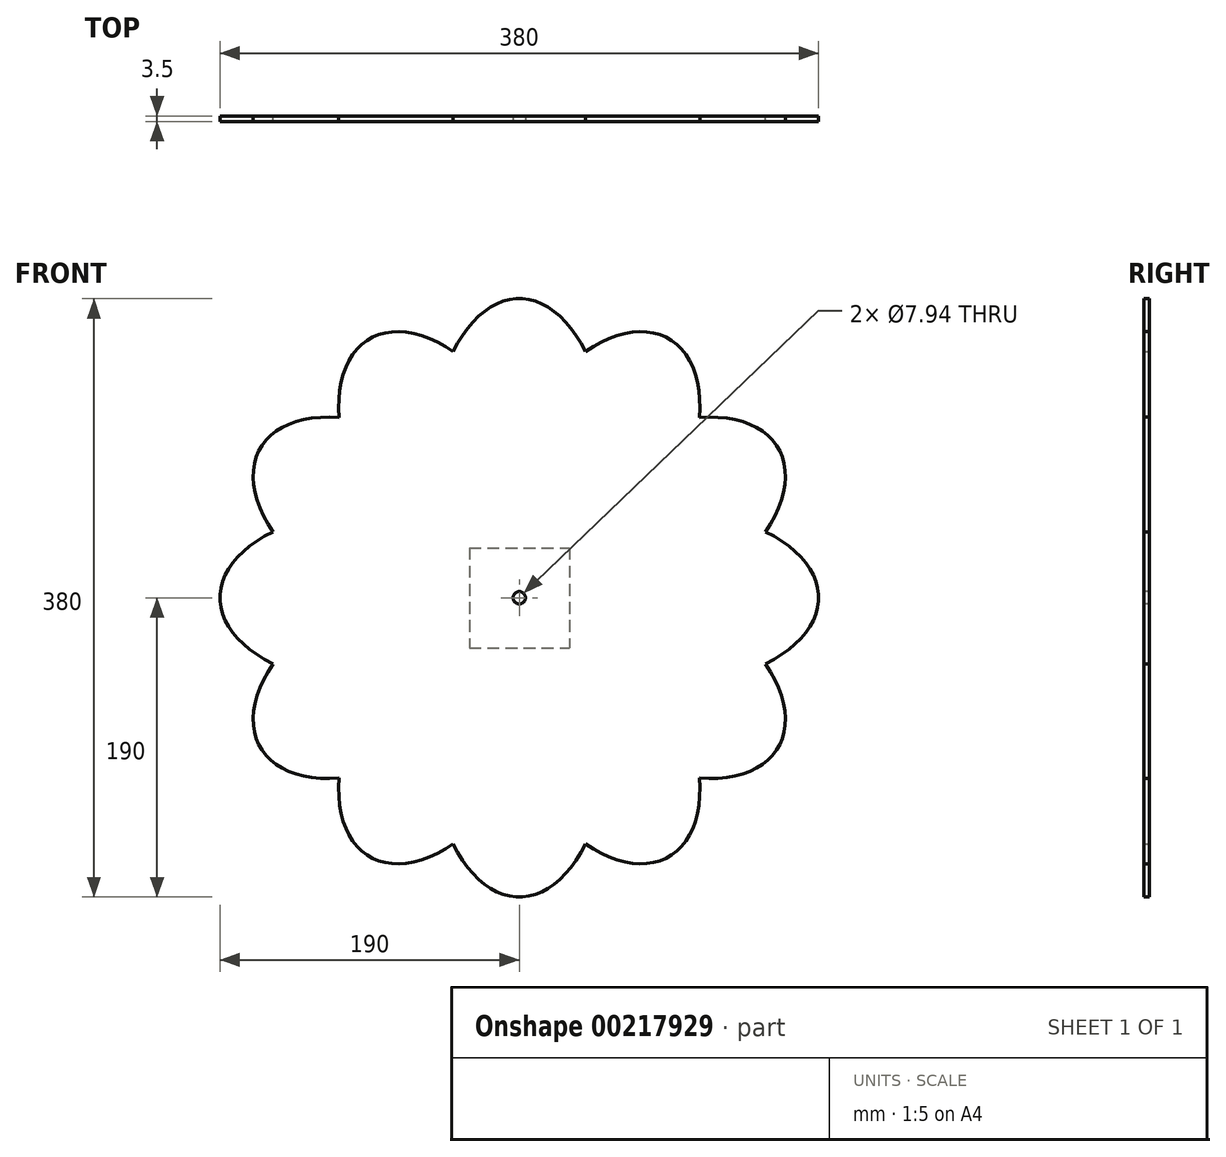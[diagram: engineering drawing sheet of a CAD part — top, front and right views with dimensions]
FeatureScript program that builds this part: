
annotation { "Feature Type Name" : "Feature", "Feature Type Description" : "" }
export const myFeature = defineFeature(function(context is Context, id is Id, definition is map)
    precondition{}
    {
        {
            var Q0;
            Q0=qCreatedBy(makeId("Front.planeOp"),FACE);
            var sketch = newSketch(context, id + "F0", { "sketchPlane" : qUnion([Q0])});
            skEllipse(sketch, "E0", {"center": v(0, 95) * mm, "majorRadius": 95 * mm, "minorRadius": 55 * mm, "majorAxis": v(0, -1)});
            skPoint(sketch, "E1.center", {"position": v(0, 0) * mm});
            skFitSpline(sketch, "E2.0", {"points": [v(-1.45, 15.04) * mm, v(0, 14.98) * mm, v(1.45, 15.04) * mm, v(3.38, 15.29) * mm, v(5.86, 15.92) * mm, v(9, 17.27) * mm, v(12.3, 19.3) * mm, v(15.72, 22.09) * mm, v(19.2, 25.66) * mm, v(22.05, 29.3) * mm, v(24.28, 32.62) * mm, v(25.92, 35.31) * mm, v(27.5, 38.18) * mm, v(29.5, 42.2) * mm, v(31.82, 47.6) * mm, v(34.25, 54.62) * mm, v(36.3, 62.08) * mm, v(37.92, 69.92) * mm, v(38.91, 76.7) * mm, v(39.47, 82.26) * mm, v(39.78, 86.46) * mm, v(39.93, 90) * mm, v(39.99, 92.86) * mm, v(40, 95) * mm, v(39.99, 97.14) * mm, v(39.93, 100) * mm, v(39.78, 103.54) * mm, v(39.47, 107.74) * mm, v(38.91, 113.3) * mm, v(37.92, 120.08) * mm, v(36.3, 127.92) * mm, v(34.25, 135.38) * mm, v(31.82, 142.4) * mm, v(29.5, 147.8) * mm, v(27.5, 151.82) * mm, v(25.92, 154.69) * mm, v(24.28, 157.38) * mm, v(22.05, 160.7) * mm, v(19.2, 164.34) * mm, v(15.72, 167.91) * mm, v(12.3, 170.7) * mm, v(9, 172.73) * mm, v(5.86, 174.08) * mm, v(3.38, 174.71) * mm, v(1.45, 174.96) * mm, v(0, 175.02) * mm, v(-1.45, 174.96) * mm, v(-3.38, 174.71) * mm, v(-5.86, 174.08) * mm, v(-9, 172.73) * mm, v(-12.3, 170.7) * mm, v(-15.72, 167.91) * mm, v(-19.2, 164.34) * mm, v(-22.05, 160.7) * mm, v(-24.28, 157.38) * mm, v(-25.92, 154.69) * mm, v(-27.5, 151.82) * mm, v(-29.5, 147.8) * mm, v(-31.82, 142.4) * mm, v(-34.25, 135.38) * mm, v(-36.3, 127.92) * mm, v(-37.92, 120.08) * mm, v(-38.91, 113.3) * mm, v(-39.47, 107.74) * mm, v(-39.78, 103.54) * mm, v(-39.93, 100) * mm, v(-39.99, 97.14) * mm, v(-40, 95) * mm, v(-39.99, 92.86) * mm, v(-39.93, 90) * mm, v(-39.78, 86.46) * mm, v(-39.47, 82.26) * mm, v(-38.91, 76.7) * mm, v(-37.92, 69.92) * mm, v(-36.3, 62.08) * mm, v(-34.25, 54.62) * mm, v(-31.82, 47.6) * mm, v(-29.5, 42.2) * mm, v(-27.5, 38.18) * mm, v(-25.92, 35.31) * mm, v(-24.28, 32.62) * mm, v(-22.05, 29.3) * mm, v(-19.2, 25.66) * mm, v(-15.72, 22.09) * mm, v(-12.3, 19.3) * mm, v(-9, 17.27) * mm, v(-5.86, 15.92) * mm, v(-3.38, 15.29) * mm, v(-1.45, 15.04) * mm, v(0, 14.98) * mm, v(1.45, 15.04) * mm, v(-1.45, 15.04) * mm]});
            skSolve(sketch);
        }
        {
            var Q0;
            Q0=makeQuery(id+"F0.imprint","IMPRINT",FACE,{"disambiguationData":[TD([[makeQuery(id+"F0.imprint","IMPRINT",EDGE,{"derivedFrom":sQuery(id+"F0.wireOp",EDGE,"E0")}),1.0]])]});
            extrude(context, id + "F1", {"entities" : qUnion([Q0]), "depth" : 3.48 * mm});
        }
        {
            var Q0;
            Q0=qCreatedBy(makeId("Right.planeOp"),FACE);
            var sketch = newSketch(context, id + "F2", { "sketchPlane" : qUnion([Q0])});
            skLineSegment(sketch, "E3", {"start": v(0, 0) * mm, "end": v(-41.22, 0) * mm});
            skSolve(sketch);
        }
        {
            var Q0;
            Q0=makeQuery(id+"F1.opExtrude","SWEPT_BODY",BODY,{"disambiguationData":[OSD([sQuery(id+"F0.wireOp",EDGE,"E0"),sQuery(id+"F0.wireOp",EDGE,"E2.0")])]});
            var Q1;
            Q1=sQuery(id+"F2.wireOp",EDGE,"E3");
            circularPattern(context, id + "F3", {"operationType" : NewBodyOperationType.ADD, "entities" : qUnion([Q0]), "axis" : qUnion([Q1]), "angle" : 360 * degree, "instanceCount" : 12, "equalSpace" : true});
        }
        {
            var Q0;
            Q0=qCreatedBy(makeId("Front.planeOp"),FACE);
            var sketch = newSketch(context, id + "F4", { "sketchPlane" : qUnion([Q0])});
            skFitSpline(sketch, "E4.0", {"points": [v(10, 17.32) * mm, v(10.54, 17) * mm, v(11.65, 16.43) * mm, v(13.42, 15.72) * mm, v(15.32, 15.14) * mm, v(18.06, 14.55) * mm, v(21.93, 14.2) * mm, v(27.37, 14.55) * mm, v(33.58, 15.79) * mm, v(39.31, 17.66) * mm, v(44.19, 19.7) * mm, v(47.97, 21.5) * mm, v(51.22, 23.23) * mm, v(53.87, 24.76) * mm, v(55.88, 25.98) * mm, v(57.91, 27.26) * mm, v(60.62, 29.07) * mm, v(64.04, 31.47) * mm, v(68.15, 34.61) * mm, v(73.63, 39.1) * mm, v(80.46, 45.3) * mm, v(88.51, 53.59) * mm, v(96.35, 62.64) * mm, v(102.62, 70.77) * mm, v(107.45, 77.58) * mm, v(110.97, 82.83) * mm, v(113.8, 87.32) * mm, v(116.01, 90.97) * mm, v(117.64, 93.74) * mm, v(119.23, 96.53) * mm, v(121.28, 100.27) * mm, v(123.75, 104.97) * mm, v(126.54, 110.64) * mm, v(130.03, 118.23) * mm, v(133.93, 127.73) * mm, v(137.85, 139.04) * mm, v(141, 150.16) * mm, v(142.95, 159.17) * mm, v(144.1, 166.17) * mm, v(144.76, 171.3) * mm, v(145.14, 175.45) * mm, v(145.34, 178.7) * mm, v(145.44, 181.1) * mm, v(145.5, 183.45) * mm, v(145.5, 186.51) * mm, v(145.37, 190.2) * mm, v(145.04, 194.37) * mm, v(144.37, 199.61) * mm, v(143.12, 205.51) * mm, v(141.09, 211.5) * mm, v(138.66, 216.39) * mm, v(136.43, 219.57) * mm, v(134.55, 221.66) * mm, v(133.1, 223.01) * mm, v(131.6, 224.18) * mm, v(130.01, 225.2) * mm, v(128.35, 226.05) * mm, v(126.58, 226.77) * mm, v(124.68, 227.35) * mm, v(121.94, 227.93) * mm, v(118.07, 228.28) * mm, v(112.63, 227.94) * mm, v(106.42, 226.7) * mm, v(100.69, 224.83) * mm, v(95.81, 222.8) * mm, v(92.03, 221) * mm, v(88.78, 219.26) * mm, v(86.13, 217.73) * mm, v(84.12, 216.5) * mm, v(82.09, 215.22) * mm, v(79.38, 213.42) * mm, v(75.96, 211.01) * mm, v(71.85, 207.88) * mm, v(66.37, 203.38) * mm, v(59.54, 197.18) * mm, v(51.49, 188.9) * mm, v(43.65, 179.85) * mm, v(37.38, 171.72) * mm, v(32.55, 164.91) * mm, v(29.03, 159.66) * mm, v(26.2, 155.17) * mm, v(23.99, 151.52) * mm, v(22.36, 148.75) * mm, v(20.77, 145.95) * mm, v(18.72, 142.22) * mm, v(16.25, 137.52) * mm, v(13.46, 131.84) * mm, v(9.97, 124.26) * mm, v(6.07, 114.76) * mm, v(2.15, 103.45) * mm, v(-1, 92.33) * mm, v(-2.95, 83.32) * mm, v(-4.1, 76.32) * mm, v(-4.76, 71.2) * mm, v(-5.14, 67.03) * mm, v(-5.34, 63.78) * mm, v(-5.44, 61.38) * mm, v(-5.5, 59.03) * mm, v(-5.5, 55.97) * mm, v(-5.37, 52.3) * mm, v(-5.04, 48.11) * mm, v(-4.37, 42.88) * mm, v(-3.12, 36.97) * mm, v(-1.09, 30.98) * mm, v(1.34, 26.1) * mm, v(3.57, 22.92) * mm, v(5.45, 20.83) * mm, v(6.9, 19.48) * mm, v(8.4, 18.3) * mm, v(9.46, 17.63) * mm, v(10, 17.32) * mm]});
            skFitSpline(sketch, "E4.1", {"points": [v(-10, 17.32) * mm, v(-9.46, 17.63) * mm, v(-8.4, 18.3) * mm, v(-6.9, 19.48) * mm, v(-5.45, 20.83) * mm, v(-3.57, 22.92) * mm, v(-1.34, 26.1) * mm, v(1.09, 30.98) * mm, v(3.12, 36.97) * mm, v(4.37, 42.88) * mm, v(5.04, 48.11) * mm, v(5.37, 52.3) * mm, v(5.5, 55.97) * mm, v(5.5, 59.03) * mm, v(5.44, 61.38) * mm, v(5.34, 63.78) * mm, v(5.14, 67.03) * mm, v(4.76, 71.2) * mm, v(4.1, 76.32) * mm, v(2.95, 83.32) * mm, v(1, 92.33) * mm, v(-2.15, 103.45) * mm, v(-6.07, 114.76) * mm, v(-9.97, 124.26) * mm, v(-13.46, 131.84) * mm, v(-16.25, 137.52) * mm, v(-18.72, 142.22) * mm, v(-20.77, 145.95) * mm, v(-22.36, 148.75) * mm, v(-23.99, 151.52) * mm, v(-26.2, 155.17) * mm, v(-29.03, 159.66) * mm, v(-32.55, 164.91) * mm, v(-37.38, 171.72) * mm, v(-43.65, 179.85) * mm, v(-51.49, 188.9) * mm, v(-59.54, 197.18) * mm, v(-66.37, 203.38) * mm, v(-71.85, 207.88) * mm, v(-75.96, 211.01) * mm, v(-79.38, 213.42) * mm, v(-82.09, 215.22) * mm, v(-84.12, 216.5) * mm, v(-86.13, 217.73) * mm, v(-88.78, 219.26) * mm, v(-92.03, 221) * mm, v(-95.81, 222.8) * mm, v(-100.69, 224.83) * mm, v(-106.42, 226.7) * mm, v(-112.63, 227.94) * mm, v(-118.07, 228.28) * mm, v(-121.94, 227.93) * mm, v(-124.68, 227.35) * mm, v(-126.58, 226.77) * mm, v(-128.35, 226.05) * mm, v(-130.01, 225.2) * mm, v(-131.6, 224.18) * mm, v(-133.1, 223.01) * mm, v(-134.55, 221.66) * mm, v(-136.43, 219.57) * mm, v(-138.66, 216.39) * mm, v(-141.09, 211.5) * mm, v(-143.12, 205.51) * mm, v(-144.37, 199.61) * mm, v(-145.04, 194.37) * mm, v(-145.37, 190.2) * mm, v(-145.5, 186.51) * mm, v(-145.5, 183.45) * mm, v(-145.44, 181.1) * mm, v(-145.34, 178.7) * mm, v(-145.14, 175.45) * mm, v(-144.76, 171.3) * mm, v(-144.1, 166.17) * mm, v(-142.95, 159.17) * mm, v(-141, 150.16) * mm, v(-137.85, 139.04) * mm, v(-133.93, 127.73) * mm, v(-130.03, 118.23) * mm, v(-126.54, 110.64) * mm, v(-123.75, 104.97) * mm, v(-121.28, 100.27) * mm, v(-119.23, 96.53) * mm, v(-117.64, 93.74) * mm, v(-116.01, 90.97) * mm, v(-113.8, 87.32) * mm, v(-110.97, 82.83) * mm, v(-107.45, 77.58) * mm, v(-102.62, 70.77) * mm, v(-96.35, 62.64) * mm, v(-88.51, 53.59) * mm, v(-80.46, 45.3) * mm, v(-73.63, 39.1) * mm, v(-68.15, 34.61) * mm, v(-64.04, 31.47) * mm, v(-60.62, 29.07) * mm, v(-57.91, 27.26) * mm, v(-55.88, 25.98) * mm, v(-53.87, 24.76) * mm, v(-51.22, 23.23) * mm, v(-47.97, 21.5) * mm, v(-44.19, 19.7) * mm, v(-39.31, 17.66) * mm, v(-33.58, 15.79) * mm, v(-27.37, 14.55) * mm, v(-21.93, 14.2) * mm, v(-18.06, 14.55) * mm, v(-15.32, 15.14) * mm, v(-13.42, 15.72) * mm, v(-11.65, 16.43) * mm, v(-10.54, 17) * mm, v(-10, 17.32) * mm]});
            skEllipticalArc(sketch, "E4.2", {});
            skEllipticalArc(sketch, "E4.3", {});
            skCircle(sketch, "E5", {"center": v(0, 0) * mm, "radius": 3.97 * mm});
            const initialGuessF4  = {"E4.2": [0.1212435565298215, 0.07, -0.8660254037844392, -0.5, 0.14, 0.075, 5.561292995522964, 5.683260991123284], "E4.3": [-0.1212435565298214, 0.07, 0.8660254037844386, -0.5, 0.14, 0.075, 0.5999243160563025, 0.7218923116632799]};
            skSetInitialGuess(sketch, initialGuessF4);
            skSolve(sketch);
        }
        {
            var Q0;
            Q0=makeQuery(id+"F4.imprint","IMPRINT",FACE,{"disambiguationData":[TD([[makeQuery(id+"F4.imprint","IMPRINT",EDGE,{"derivedFrom":sQuery(id+"F4.wireOp",EDGE,"E5")}),1.0]])]});
            extrude(context, id + "F5", {"entities" : qUnion([Q0]), "operationType" : NewBodyOperationType.REMOVE, "oppositeDirection" : true, "depth" : 50 * mm, "symmetric" : true});
        }
        {
            var Q0;
            {var subQ0=makeQuery(id+"F1.opExtrude","CAP_FACE",FACE,{"disambiguationData":[OSD([sQuery(id+"F0.wireOp",EDGE,"E0"),sQuery(id+"F0.wireOp",EDGE,"E2.0")])],"isStart":true});Q0=makeQuery(id+"F3.boolean.opBoolean","MERGE",FACE,{"derivedFrom":[subQ0,makeQuery(id+"F3.opPattern","COPY",FACE,{"derivedFrom":subQ0,"instanceName":"1"}),makeQuery(id+"F3.opPattern","COPY",FACE,{"derivedFrom":subQ0,"instanceName":"2"}),makeQuery(id+"F3.opPattern","COPY",FACE,{"derivedFrom":subQ0,"instanceName":"3"}),makeQuery(id+"F3.opPattern","COPY",FACE,{"derivedFrom":subQ0,"instanceName":"4"}),makeQuery(id+"F3.opPattern","COPY",FACE,{"derivedFrom":subQ0,"instanceName":"5"}),makeQuery(id+"F3.opPattern","COPY",FACE,{"derivedFrom":subQ0,"instanceName":"6"}),makeQuery(id+"F3.opPattern","COPY",FACE,{"derivedFrom":subQ0,"instanceName":"7"}),makeQuery(id+"F3.opPattern","COPY",FACE,{"derivedFrom":subQ0,"instanceName":"8"}),makeQuery(id+"F3.opPattern","COPY",FACE,{"derivedFrom":subQ0,"instanceName":"9"}),makeQuery(id+"F3.opPattern","COPY",FACE,{"derivedFrom":subQ0,"instanceName":"10"}),makeQuery(id+"F3.opPattern","COPY",FACE,{"derivedFrom":subQ0,"instanceName":"11"})]});}
            var sketch = newSketch(context, id + "F6", { "sketchPlane" : qUnion([Q0])});
            skLineSegment(sketch, "E6.bottom", {"start": v(31.75, 31.75) * mm, "end": v(-31.75, 31.75) * mm});
            skLineSegment(sketch, "E6.top", {"start": v(31.75, -31.75) * mm, "end": v(-31.75, -31.75) * mm});
            skLineSegment(sketch, "E6.left", {"start": v(31.75, 31.75) * mm, "end": v(31.75, -31.75) * mm});
            skLineSegment(sketch, "E6.right", {"start": v(-31.75, 31.75) * mm, "end": v(-31.75, -31.75) * mm});
            skPoint(sketch, "E7", {"position": v(-31.75, 0) * mm});
            skPoint(sketch, "E8", {"position": v(0, -31.75) * mm});
            skSolve(sketch);
        }
        {
            var Q0;
            {var subQ0=sQuery(id+"F0.wireOp",EDGE,"E2.0");var subQ1=sQuery(id+"F0.wireOp",EDGE,"E0");var subQ2=makeQuery(id+"F1.opExtrude","CAP_FACE",FACE,{"disambiguationData":[OSD([subQ1,subQ0])],"isStart":true});var subQ3=makeQuery(id+"F3.opPattern","COPY",FACE,{"derivedFrom":subQ2,"instanceName":"7"});var subQ4=makeQuery(id+"F3.opPattern","COPY",FACE,{"derivedFrom":subQ2,"instanceName":"1"});var subQ5=makeQuery(id+"F3.opPattern","COPY",FACE,{"derivedFrom":subQ2,"instanceName":"6"});var subQ6=makeQuery(id+"F3.opPattern","COPY",FACE,{"derivedFrom":subQ2,"instanceName":"5"});var subQ7=makeQuery(id+"F3.opPattern","COPY",FACE,{"derivedFrom":subQ2,"instanceName":"4"});var subQ8=makeQuery(id+"F3.opPattern","COPY",FACE,{"derivedFrom":subQ2,"instanceName":"2"});var subQ9=makeQuery(id+"F3.opPattern","COPY",FACE,{"derivedFrom":subQ2,"instanceName":"8"});var subQ10=makeQuery(id+"F3.opPattern","COPY",FACE,{"derivedFrom":subQ2,"instanceName":"3"});var subQ15=makeQuery(id+"F3.opPattern","COPY",FACE,{"derivedFrom":subQ2,"instanceName":"9"});var subQ17=makeQuery(id+"F3.opPattern","COPY",FACE,{"derivedFrom":subQ2,"instanceName":"11"});var subQ18=makeQuery(id+"F3.opPattern","COPY",FACE,{"derivedFrom":subQ2,"instanceName":"10"});Q0=makeQuery(id+"F6.imprint","IMPRINT",FACE,{"disambiguationData":[TD([[makeQuery(id+"F6.imprint","IMPRINT",EDGE,{"derivedFrom":makeQuery(id+"F5.boolean.opBoolean","INTERSECT",EDGE,{"derivedFrom":[makeQuery(id+"F3.boolean.opBoolean","MERGE",FACE,{"derivedFrom":[subQ2,subQ4,subQ8,subQ10,subQ7,subQ6,subQ5,subQ3,subQ9,subQ15,subQ18,subQ17]}),makeQuery(id+"F5.opExtrude","SWEPT_FACE",FACE,{"disambiguationData":[OSD([sQuery(id+"F4.wireOp",EDGE,"E5")])]})]})}),1.0]])]});}
            extrude(context, id + "F7", {"entities" : qUnion([Q0]), "depth" : 5 / 203.2 * mm});
        }
    });
